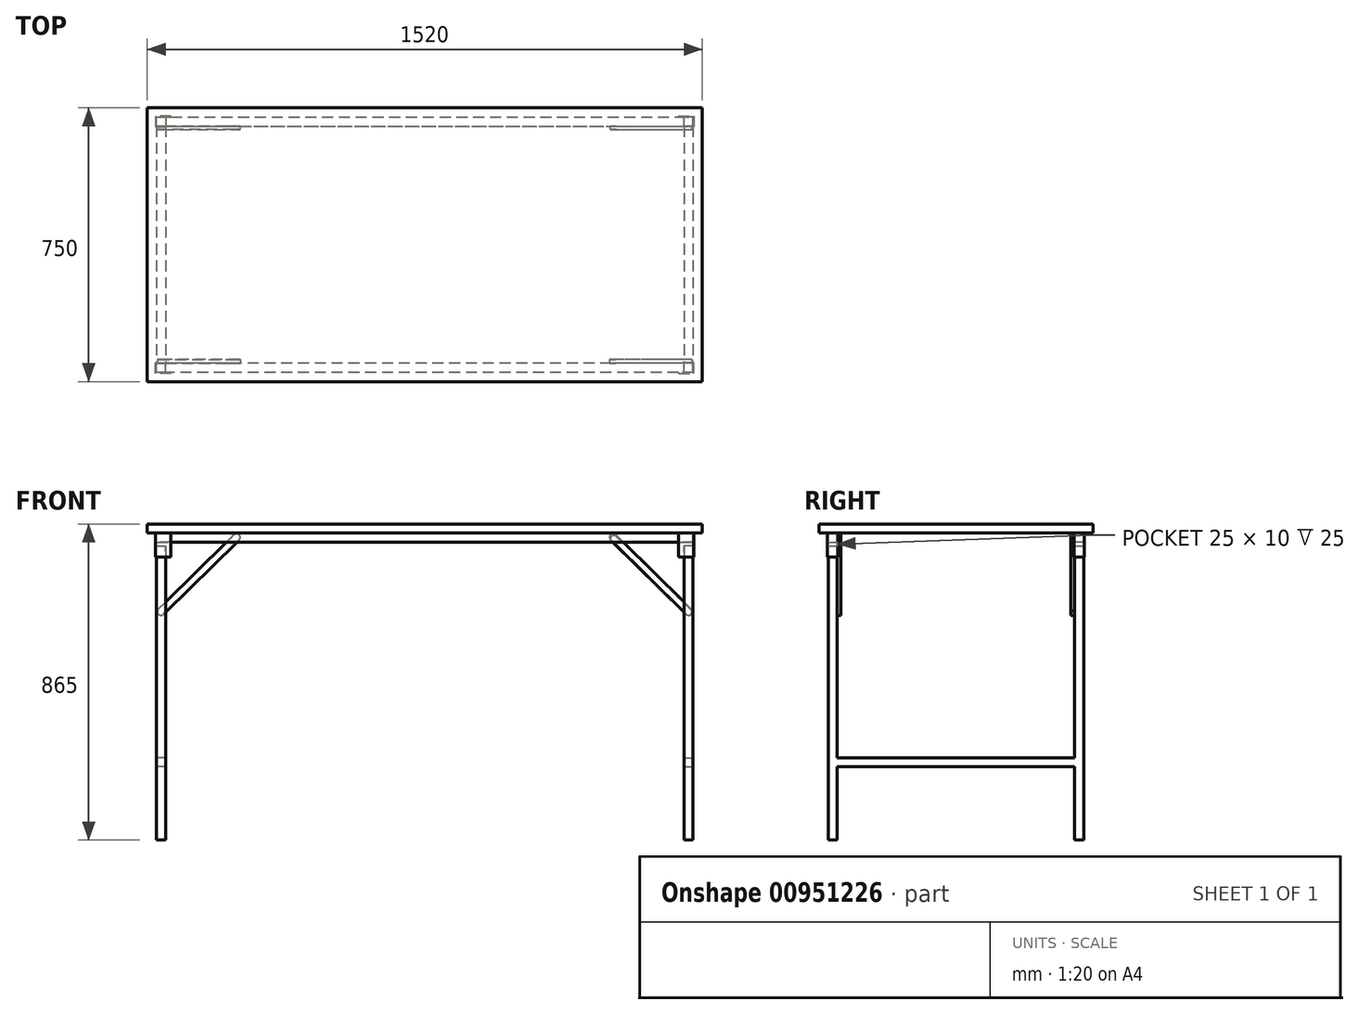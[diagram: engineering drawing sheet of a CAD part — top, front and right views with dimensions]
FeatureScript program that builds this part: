
annotation { "Feature Type Name" : "Feature", "Feature Type Description" : "" }
export const myFeature = defineFeature(function(context is Context, id is Id, definition is map)
    precondition{}
    {
        {
            var Q0;
            Q0=qCreatedBy(makeId("Top.planeOp"),FACE);
            var sketch = newSketch(context, id + "F0", { "sketchPlane" : qUnion([Q0])});
            skLineSegment(sketch, "E0.bottom", {"start": v(0, 0) * mm, "end": v(-1520, 0) * mm});
            skLineSegment(sketch, "E0.top", {"start": v(0, 750) * mm, "end": v(-1520, 750) * mm});
            skLineSegment(sketch, "E0.left", {"start": v(0, 0) * mm, "end": v(0, 750) * mm});
            skLineSegment(sketch, "E0.right", {"start": v(-1520, 0) * mm, "end": v(-1520, 750) * mm});
            skSolve(sketch);
        }
        {
            var Q0;
            Q0=makeQuery(id+"F0.imprint","IMPRINT",FACE,{"disambiguationData":[TD([[makeQuery(id+"F0.imprint","IMPRINT",EDGE,{"derivedFrom":sQuery(id+"F0.wireOp",EDGE,"E0.bottom")}),-1.0]])]});
            extrude(context, id + "F1", {"entities" : qUnion([Q0]), "depth" : 25 * mm, "offsetDistance" : 25 * mm});
        }
        {
            var Q0;
            Q0=makeQuery(id+"F1.opExtrude","CAP_FACE",FACE,{"disambiguationData":[OSD([sQuery(id+"F0.wireOp",EDGE,"E0.bottom"),sQuery(id+"F0.wireOp",EDGE,"E0.top"),sQuery(id+"F0.wireOp",EDGE,"E0.left"),sQuery(id+"F0.wireOp",EDGE,"E0.right")])],"isStart":true});
            var sketch = newSketch(context, id + "F2", { "sketchPlane" : qUnion([Q0])});
            skLineSegment(sketch, "E1.bottom", {"start": v(-25, -25) * mm, "end": v(-1495, -25) * mm});
            skLineSegment(sketch, "E1.top", {"start": v(-25, -50) * mm, "end": v(-1495, -50) * mm});
            skLineSegment(sketch, "E1.left", {"start": v(-25, -25) * mm, "end": v(-25, -50) * mm});
            skLineSegment(sketch, "E1.right", {"start": v(-1495, -25) * mm, "end": v(-1495, -50) * mm});
            skLineSegment(sketch, "E2.bottom", {"start": v(-1495, -700) * mm, "end": v(-25, -700) * mm});
            skLineSegment(sketch, "E2.top", {"start": v(-1495, -725) * mm, "end": v(-25, -725) * mm});
            skLineSegment(sketch, "E2.left", {"start": v(-1495, -700) * mm, "end": v(-1495, -725) * mm});
            skLineSegment(sketch, "E2.right", {"start": v(-25, -700) * mm, "end": v(-25, -725) * mm});
            skSolve(sketch);
        }
        {
            var Q0;
            Q0=qSketchRegion(id+"F2",true);
            extrude(context, id + "F3", {"entities" : qUnion([Q0]), "operationType" : NewBodyOperationType.ADD, "depth" : 25 * mm, "offsetDistance" : 25 * mm});
        }
        {
            var Q0;
            Q0=makeQuery(id+"F1.opExtrude","CAP_FACE",FACE,{"disambiguationData":[OSD([sQuery(id+"F0.wireOp",EDGE,"E0.bottom"),sQuery(id+"F0.wireOp",EDGE,"E0.top"),sQuery(id+"F0.wireOp",EDGE,"E0.left"),sQuery(id+"F0.wireOp",EDGE,"E0.right")])],"isStart":true});
            var sketch = newSketch(context, id + "F4", { "sketchPlane" : qUnion([Q0])});
            skLineSegment(sketch, "E3", {"start": v(-25, -25) * mm, "end": v(-65, -25) * mm});
            skLineSegment(sketch, "E4", {"start": v(-65, -25) * mm, "end": v(-65, -23) * mm});
            skLineSegment(sketch, "E5", {"start": v(-65, -23) * mm, "end": v(-23, -23) * mm});
            skLineSegment(sketch, "E6", {"start": v(-23, -23) * mm, "end": v(-23, -52) * mm});
            skLineSegment(sketch, "E7", {"start": v(-23, -52) * mm, "end": v(-65, -52) * mm});
            skLineSegment(sketch, "E8", {"start": v(-65, -52) * mm, "end": v(-65, -50) * mm});
            skLineSegment(sketch, "E9", {"start": v(-65, -50) * mm, "end": v(-25, -50) * mm});
            skLineSegment(sketch, "E10", {"start": v(-25, -50) * mm, "end": v(-25, -25) * mm});
            skSolve(sketch);
        }
        {
            var Q0;
            Q0=makeQuery(id+"F4.imprint","IMPRINT",FACE,{"disambiguationData":[TD([[makeQuery(id+"F4.imprint","IMPRINT",EDGE,{"derivedFrom":sQuery(id+"F4.wireOp",EDGE,"E3")}),-1.0]])]});
            extrude(context, id + "F5", {"entities" : qUnion([Q0]), "operationType" : NewBodyOperationType.ADD, "depth" : 65 * mm, "offsetDistance" : 25 * mm});
        }
        {
            var Q0;
            Q0=makeQuery(id+"F3.opExtrude","CAP_FACE",FACE,{"disambiguationData":[OSD([sQuery(id+"F2.wireOp",EDGE,"E1.bottom"),sQuery(id+"F2.wireOp",EDGE,"E1.top"),sQuery(id+"F2.wireOp",EDGE,"E1.left"),sQuery(id+"F2.wireOp",EDGE,"E1.right")])],"isStart":false});
            cPlane(context, id + "F6", {"entities" : qUnion([Q0]), "cplaneType" : CPlaneType.OFFSET, "offset" : 10 * mm, "width" : 150 * mm, "height" : 150 * mm});
        }
        {
            var Q0;
            Q0=qCreatedBy(id+"F6.planeOp",FACE);
            var sketch = newSketch(context, id + "F7", { "sketchPlane" : qUnion([Q0])});
            skLineSegment(sketch, "E11.bottom", {"start": v(-25, -25.02) * mm, "end": v(-50, -25.02) * mm});
            skLineSegment(sketch, "E11.top", {"start": v(-25, -50.02) * mm, "end": v(-50, -50.02) * mm});
            skLineSegment(sketch, "E11.left", {"start": v(-25, -25.02) * mm, "end": v(-25, -50.02) * mm});
            skLineSegment(sketch, "E11.right", {"start": v(-50, -25.02) * mm, "end": v(-50, -50.02) * mm});
            skSolve(sketch);
        }
        {
            var Q0;
            Q0=makeQuery(id+"F7.imprint","IMPRINT",FACE,{"disambiguationData":[TD([[makeQuery(id+"F7.imprint","IMPRINT",EDGE,{"derivedFrom":sQuery(id+"F7.wireOp",EDGE,"E11.bottom")}),1.0]])]});
            extrude(context, id + "F8", {"entities" : qUnion([Q0]), "operationType" : NewBodyOperationType.ADD, "depth" : 805 * mm, "offsetDistance" : 25 * mm});
        }
        {
            var Q0;
            Q0=makeQuery(id+"F0.imprint","IMPRINT",FACE,{"disambiguationData":[TD([[makeQuery(id+"F0.imprint","IMPRINT",EDGE,{"derivedFrom":sQuery(id+"F0.wireOp",EDGE,"E0.bottom")}),-1.0]])]});
            var sketch = newSketch(context, id + "F9", { "sketchPlane" : qUnion([Q0])});
            skLineSegment(sketch, "E12", {"start": v(-1495, 25) * mm, "end": v(-1455, 25) * mm});
            skLineSegment(sketch, "E13", {"start": v(-1455, 25) * mm, "end": v(-1455, 23) * mm});
            skLineSegment(sketch, "E14", {"start": v(-1455, 23) * mm, "end": v(-1497, 23) * mm});
            skLineSegment(sketch, "E15", {"start": v(-1497, 23) * mm, "end": v(-1497, 52) * mm});
            skLineSegment(sketch, "E16", {"start": v(-1497, 52) * mm, "end": v(-1455, 52) * mm});
            skLineSegment(sketch, "E17", {"start": v(-1455, 52) * mm, "end": v(-1455, 50) * mm});
            skLineSegment(sketch, "E18", {"start": v(-1455, 50) * mm, "end": v(-1495, 50) * mm});
            skLineSegment(sketch, "E19", {"start": v(-1495, 50) * mm, "end": v(-1495, 25) * mm});
            skLineSegment(sketch, "E20.MirrorCS", {"start": v(-1455, 724.98) * mm, "end": v(-1455, 726.98) * mm});
            skLineSegment(sketch, "E21.MirrorCS", {"start": v(-1455, 697.98) * mm, "end": v(-1455, 699.98) * mm});
            skLineSegment(sketch, "E22.MirrorCS", {"start": v(-1497, 697.98) * mm, "end": v(-1455, 697.98) * mm});
            skLineSegment(sketch, "E23.MirrorCS", {"start": v(-1455, 699.98) * mm, "end": v(-1495, 699.98) * mm});
            skLineSegment(sketch, "E24.MirrorCS", {"start": v(-1495, 724.98) * mm, "end": v(-1455, 724.98) * mm});
            skLineSegment(sketch, "E25.MirrorCS", {"start": v(-1455, 726.98) * mm, "end": v(-1497, 726.98) * mm});
            skLineSegment(sketch, "E26.MirrorCS", {"start": v(-1497, 726.98) * mm, "end": v(-1497, 697.98) * mm});
            skLineSegment(sketch, "E27.MirrorCS", {"start": v(-1495, 699.98) * mm, "end": v(-1495, 724.98) * mm});
            skLineSegment(sketch, "E28.MirrorCS", {"start": v(-65.05, 724.98) * mm, "end": v(-65.05, 726.98) * mm});
            skLineSegment(sketch, "E29.MirrorCS", {"start": v(-65.05, 697.98) * mm, "end": v(-65.05, 699.98) * mm});
            skLineSegment(sketch, "E30.MirrorCS", {"start": v(-23.05, 726.98) * mm, "end": v(-23.05, 697.98) * mm});
            skLineSegment(sketch, "E31.MirrorCS", {"start": v(-65.05, 699.98) * mm, "end": v(-25.05, 699.98) * mm});
            skLineSegment(sketch, "E32.MirrorCS", {"start": v(-25.05, 699.98) * mm, "end": v(-25.05, 724.98) * mm});
            skLineSegment(sketch, "E33.MirrorCS", {"start": v(-65.05, 726.98) * mm, "end": v(-23.05, 726.98) * mm});
            skLineSegment(sketch, "E34.MirrorCS", {"start": v(-25.05, 724.98) * mm, "end": v(-65.05, 724.98) * mm});
            skLineSegment(sketch, "E35.MirrorCS", {"start": v(-23.05, 697.98) * mm, "end": v(-65.05, 697.98) * mm});
            skSolve(sketch);
        }
        {
            var Q0;
            Q0=makeQuery(id+"F9.imprint","IMPRINT",FACE,{"disambiguationData":[TD([[makeQuery(id+"F9.imprint","IMPRINT",EDGE,{"derivedFrom":sQuery(id+"F9.wireOp",EDGE,"E20.MirrorCS")}),1.0]])]});
            var Q1;
            Q1=makeQuery(id+"F9.imprint","IMPRINT",FACE,{"disambiguationData":[TD([[makeQuery(id+"F9.imprint","IMPRINT",EDGE,{"derivedFrom":sQuery(id+"F9.wireOp",EDGE,"E28.MirrorCS")}),-1.0]])]});
            var Q2;
            Q2=makeQuery(id+"F9.imprint","IMPRINT",FACE,{"disambiguationData":[TD([[makeQuery(id+"F9.imprint","IMPRINT",EDGE,{"derivedFrom":sQuery(id+"F9.wireOp",EDGE,"E12")}),-1.0]])]});
            extrude(context, id + "F10", {"entities" : qUnion([Q0, Q1, Q2]), "operationType" : NewBodyOperationType.ADD, "oppositeDirection" : true, "depth" : 65 * mm, "offsetDistance" : 25 * mm});
        }
        {
            var Q0;
            Q0=makeQuery(id+"F3.opExtrude","CAP_FACE",FACE,{"disambiguationData":[OSD([sQuery(id+"F2.wireOp",EDGE,"E1.bottom"),sQuery(id+"F2.wireOp",EDGE,"E1.top"),sQuery(id+"F2.wireOp",EDGE,"E1.left"),sQuery(id+"F2.wireOp",EDGE,"E1.right")])],"isStart":false});
            cPlane(context, id + "F11", {"entities" : qUnion([Q0]), "cplaneType" : CPlaneType.OFFSET, "offset" : 10 * mm, "width" : 150 * mm, "height" : 150 * mm});
        }
        {
            var Q0;
            Q0=qCreatedBy(id+"F11.planeOp",FACE);
            var sketch = newSketch(context, id + "F12", { "sketchPlane" : qUnion([Q0])});
            skLineSegment(sketch, "E36.bottom", {"start": v(-1470, -25) * mm, "end": v(-1495, -25) * mm});
            skLineSegment(sketch, "E36.top", {"start": v(-1470, -50) * mm, "end": v(-1495, -50) * mm});
            skLineSegment(sketch, "E36.left", {"start": v(-1470, -25) * mm, "end": v(-1470, -50) * mm});
            skLineSegment(sketch, "E36.right", {"start": v(-1495, -25) * mm, "end": v(-1495, -50) * mm});
            skSolve(sketch);
        }
        {
            var Q0;
            Q0=makeQuery(id+"F12.imprint","IMPRINT",FACE,{"disambiguationData":[TD([[makeQuery(id+"F12.imprint","IMPRINT",EDGE,{"derivedFrom":sQuery(id+"F12.wireOp",EDGE,"E36.bottom")}),1.0]])]});
            extrude(context, id + "F13", {"entities" : qUnion([Q0]), "operationType" : NewBodyOperationType.ADD, "depth" : 805 * mm, "offsetDistance" : 25 * mm});
        }
        {
            var Q0;
            Q0=makeQuery(id+"F3.opExtrude","CAP_FACE",FACE,{"disambiguationData":[OSD([sQuery(id+"F2.wireOp",EDGE,"E2.bottom"),sQuery(id+"F2.wireOp",EDGE,"E2.top"),sQuery(id+"F2.wireOp",EDGE,"E2.left"),sQuery(id+"F2.wireOp",EDGE,"E2.right")])],"isStart":false});
            cPlane(context, id + "F14", {"entities" : qUnion([Q0]), "cplaneType" : CPlaneType.OFFSET, "offset" : 10 * mm, "width" : 150 * mm, "height" : 150 * mm});
        }
        {
            var Q0;
            Q0=qCreatedBy(id+"F14.planeOp",FACE);
            var sketch = newSketch(context, id + "F15", { "sketchPlane" : qUnion([Q0])});
            skLineSegment(sketch, "E37.bottom", {"start": v(-25, -700) * mm, "end": v(-50, -700) * mm});
            skLineSegment(sketch, "E37.top", {"start": v(-25, -725) * mm, "end": v(-50, -725) * mm});
            skLineSegment(sketch, "E37.left", {"start": v(-25, -700) * mm, "end": v(-25, -725) * mm});
            skLineSegment(sketch, "E37.right", {"start": v(-50, -700) * mm, "end": v(-50, -725) * mm});
            skLineSegment(sketch, "E38.bottom", {"start": v(-1495, -725) * mm, "end": v(-1470, -725) * mm});
            skLineSegment(sketch, "E38.top", {"start": v(-1495, -700) * mm, "end": v(-1470, -700) * mm});
            skLineSegment(sketch, "E38.left", {"start": v(-1495, -725) * mm, "end": v(-1495, -700) * mm});
            skLineSegment(sketch, "E38.right", {"start": v(-1470, -725) * mm, "end": v(-1470, -700) * mm});
            skSolve(sketch);
        }
        {
            var Q0;
            Q0=qSketchRegion(id+"F15",true);
            extrude(context, id + "F16", {"entities" : qUnion([Q0]), "operationType" : NewBodyOperationType.ADD, "depth" : 805 * mm, "offsetDistance" : 25 * mm});
        }
        {
            var Q0;
            Q0=makeQuery(id+"F8.opExtrude","SWEPT_FACE",FACE,{"disambiguationData":[OSD([sQuery(id+"F7.wireOp",EDGE,"E11.top")])]});
            cPlane(context, id + "F17", {"entities" : qUnion([Q0]), "cplaneType" : CPlaneType.OFFSET, "offset" : 0 * mm, "width" : 150 * mm, "height" : 150 * mm});
        }
        {
            var Q0;
            Q0=qCreatedBy(id+"F17.planeOp",FACE);
            var sketch = newSketch(context, id + "F18", { "sketchPlane" : qUnion([Q0])});
            skLineSegment(sketch, "E39.bottom", {"start": v(25, -615) * mm, "end": v(50, -615) * mm});
            skLineSegment(sketch, "E39.top", {"start": v(25, -640) * mm, "end": v(50, -640) * mm});
            skLineSegment(sketch, "E39.left", {"start": v(25, -615) * mm, "end": v(25, -640) * mm});
            skLineSegment(sketch, "E39.right", {"start": v(50, -615) * mm, "end": v(50, -640) * mm});
            skSolve(sketch);
        }
        {
            var Q0;
            Q0=makeQuery(id+"F18.imprint","IMPRINT",FACE,{"disambiguationData":[TD([[makeQuery(id+"F18.imprint","IMPRINT",EDGE,{"derivedFrom":sQuery(id+"F18.wireOp",EDGE,"E39.bottom")}),-1.0]])]});
            extrude(context, id + "F19", {"entities" : qUnion([Q0]), "operationType" : NewBodyOperationType.ADD, "depth" : 650 * mm, "offsetDistance" : 25 * mm});
        }
        {
            var Q0;
            Q0=makeQuery(id+"F13.opExtrude","SWEPT_FACE",FACE,{"disambiguationData":[OSD([sQuery(id+"F12.wireOp",EDGE,"E36.top")])]});
            cPlane(context, id + "F20", {"entities" : qUnion([Q0]), "cplaneType" : CPlaneType.OFFSET, "offset" : 0 * mm, "width" : 150 * mm, "height" : 150 * mm});
        }
        {
            var Q0;
            Q0=qCreatedBy(id+"F20.planeOp",FACE);
            var sketch = newSketch(context, id + "F21", { "sketchPlane" : qUnion([Q0])});
            skLineSegment(sketch, "E40.0", {"start": v(1470, -840) * mm, "end": v(1470, -65) * mm});
            skLineSegment(sketch, "E41.0.0", {"start": v(1495, -65) * mm, "end": v(1470, -65) * mm});
            skLineSegment(sketch, "E41.0.1", {"start": v(1470, -65) * mm, "end": v(1470, -840) * mm});
            skLineSegment(sketch, "E41.0.2", {"start": v(1470, -840) * mm, "end": v(1495, -840) * mm});
            skLineSegment(sketch, "E41.0.3", {"start": v(1495, -840) * mm, "end": v(1495, -65) * mm});
            skLineSegment(sketch, "E42.bottom", {"start": v(1470, -615) * mm, "end": v(1495, -615) * mm});
            skLineSegment(sketch, "E42.top", {"start": v(1470, -640) * mm, "end": v(1495, -640) * mm});
            skLineSegment(sketch, "E42.left", {"start": v(1470, -615) * mm, "end": v(1470, -640) * mm});
            skLineSegment(sketch, "E42.right", {"start": v(1495, -615) * mm, "end": v(1495, -640) * mm});
            skSolve(sketch);
        }
        {
            var Q0;
            Q0=makeQuery(id+"F21.imprint","IMPRINT",FACE,{"disambiguationData":[TD([[makeQuery(id+"F21.imprint","IMPRINT",EDGE,{"derivedFrom":sQuery(id+"F21.wireOp",EDGE,"E42.bottom")}),-1.0]])]});
            extrude(context, id + "F22", {"entities" : qUnion([Q0]), "operationType" : NewBodyOperationType.ADD, "depth" : 650 * mm, "offsetDistance" : 25 * mm});
        }
        {
            var Q0;
            {var subQ0=sQuery(id+"F9.wireOp",EDGE,"E32.MirrorCS");var subQ3=sQuery(id+"F15.wireOp",EDGE,"E37.bottom");Q0=makeQuery(id+"F19.boolean.opBoolean","SPLIT",FACE,{"disambiguationData":[TD([makeQuery(id+"F10.opExtrude","SWEPT_FACE",FACE,{"disambiguationData":[OSD([subQ0])]})])],"derivedFrom":makeQuery(id+"F16.opExtrude","SWEPT_FACE",FACE,{"disambiguationData":[OSD([subQ3])]})});}
            var sketch = newSketch(context, id + "F23", { "sketchPlane" : qUnion([Q0])});
            skPoint(sketch, "E43", {"position": v(-37.5, -215) * mm});
            skPoint(sketch, "E44", {"position": v(-243.05, -12.5) * mm});
            skPoint(sketch, "E45", {"position": v(-118.3, 56.79) * mm});
            skLineSegment(sketch, "E46", {"start": v(-234.62, -9.28) * mm, "end": v(-27.8, -212.56) * mm});
            skLineSegment(sketch, "E47", {"start": v(-251.33, -18.85) * mm, "end": v(-44.5, -222.13) * mm});
            skArc(sketch, "E48", {"start": v(-44.5, -222.13) * mm, "mid": v(-32.53, -223.68) * mm, "end": v(-27.8, -212.56) * mm});
            skArc(sketch, "E49", {"start": v(-234.62, -9.28) * mm, "mid": v(-246.6, -7.73) * mm, "end": v(-251.33, -18.85) * mm});
            skSolve(sketch);
        }
        {
            var Q0;
            {var subQ0=sQuery(id+"F23.wireOp",EDGE,"E49");Q0=makeQuery(id+"F23.imprint","IMPRINT",FACE,{"disambiguationData":[TD([[makeQuery(id+"F23.imprint","IMPRINT",EDGE,{"derivedFrom":subQ0}),1.0]])]});}
            var Q1;
            {var subQ0=sQuery(id+"F23.wireOp",EDGE,"E48");Q1=makeQuery(id+"F23.imprint","IMPRINT",FACE,{"disambiguationData":[TD([[makeQuery(id+"F23.imprint","IMPRINT",EDGE,{"derivedFrom":subQ0}),1.0]])]});}
            extrude(context, id + "F24", {"entities" : qUnion([Q0, Q1]), "operationType" : NewBodyOperationType.ADD, "depth" : 10 * mm, "offsetDistance" : 25 * mm});
        }
        {
            var Q0;
            Q0=makeQuery(id+"F19.boolean.opBoolean","SPLIT",FACE,{"disambiguationData":[TD([makeQuery(id+"F19.opExtrude","SWEPT_FACE",FACE,{"disambiguationData":[OSD([sQuery(id+"F18.wireOp",EDGE,"E39.bottom")])]})])],"derivedFrom":makeQuery(id+"F8.opExtrude","SWEPT_FACE",FACE,{"disambiguationData":[OSD([sQuery(id+"F7.wireOp",EDGE,"E11.top")])]})});
            var sketch = newSketch(context, id + "F25", { "sketchPlane" : qUnion([Q0])});
            skPoint(sketch, "E50", {"position": v(37.5, -215) * mm});
            skPoint(sketch, "E51", {"position": v(243, -12.5) * mm});
            skLineSegment(sketch, "E52", {"start": v(44.52, -222.12) * mm, "end": v(250.98, -18.46) * mm});
            skLineSegment(sketch, "E53", {"start": v(30.48, -207.88) * mm, "end": v(236.93, -4.22) * mm});
            skLineSegment(sketch, "E54", {"start": v(43.27, -207.6) * mm, "end": v(43.27, -207.6) * mm});
            skArc(sketch, "E55", {"start": v(30.48, -207.88) * mm, "mid": v(30.38, -222.02) * mm, "end": v(44.52, -222.12) * mm});
            skArc(sketch, "E56", {"start": v(250.98, -18.46) * mm, "mid": v(251.08, -4.32) * mm, "end": v(236.93, -4.22) * mm});
            skSolve(sketch);
        }
        {
            var Q0;
            {var subQ0=sQuery(id+"F25.wireOp",EDGE,"E56");Q0=makeQuery(id+"F25.imprint","IMPRINT",FACE,{"disambiguationData":[TD([[makeQuery(id+"F25.imprint","IMPRINT",EDGE,{"derivedFrom":subQ0}),1.0]])]});}
            var Q1;
            {var subQ0=sQuery(id+"F25.wireOp",EDGE,"E55");Q1=makeQuery(id+"F25.imprint","IMPRINT",FACE,{"disambiguationData":[TD([[makeQuery(id+"F25.imprint","IMPRINT",EDGE,{"derivedFrom":subQ0}),1.0]])]});}
            extrude(context, id + "F26", {"entities" : qUnion([Q0, Q1]), "depth" : 10 * mm, "offsetDistance" : 25 * mm});
        }
        {
            var Q0;
            {var subQ2=sQuery(id+"F15.wireOp",EDGE,"E38.top");var subQ3=sQuery(id+"F9.wireOp",EDGE,"E27.MirrorCS");Q0=makeQuery(id+"F22.boolean.opBoolean","SPLIT",FACE,{"disambiguationData":[TD([makeQuery(id+"F10.opExtrude","SWEPT_FACE",FACE,{"disambiguationData":[OSD([subQ3])]})])],"derivedFrom":makeQuery(id+"F16.opExtrude","SWEPT_FACE",FACE,{"disambiguationData":[OSD([subQ2])]})});}
            cPlane(context, id + "F27", {"entities" : qUnion([Q0]), "cplaneType" : CPlaneType.OFFSET, "offset" : 0 * mm, "width" : 150 * mm, "height" : 150 * mm});
        }
        {
            var Q0;
            Q0=qCreatedBy(id+"F27.planeOp",FACE);
            var sketch = newSketch(context, id + "F28", { "sketchPlane" : qUnion([Q0])});
            skPoint(sketch, "E57", {"position": v(-1482.5, -215) * mm});
            skPoint(sketch, "E58", {"position": v(-1277, -12.5) * mm});
            skLineSegment(sketch, "E59", {"start": v(-1282.53, -4.73) * mm, "end": v(-1489.5, -207.86) * mm});
            skLineSegment(sketch, "E60", {"start": v(-1475.5, -222.14) * mm, "end": v(-1268.52, -19) * mm});
            skArc(sketch, "E61", {"start": v(-1489.5, -207.86) * mm, "mid": v(-1489.64, -222) * mm, "end": v(-1475.5, -222.14) * mm});
            skArc(sketch, "E62", {"start": v(-1268.52, -19) * mm, "mid": v(-1268.39, -4.87) * mm, "end": v(-1282.53, -4.73) * mm});
            skSolve(sketch);
        }
        {
            var Q0;
            Q0=makeQuery(id+"F28.imprint","IMPRINT",FACE,{"disambiguationData":[TD([[makeQuery(id+"F28.imprint","IMPRINT",EDGE,{"derivedFrom":sQuery(id+"F28.wireOp",EDGE,"E59")}),1.0]])]});
            extrude(context, id + "F29", {"entities" : qUnion([Q0]), "operationType" : NewBodyOperationType.ADD, "depth" : 10 * mm, "offsetDistance" : 25 * mm});
        }
        {
            var Q0;
            {var subQ0=sQuery(id+"F21.wireOp",EDGE,"E41.0.0");Q0=makeQuery(id+"F21.imprint","IMPRINT",FACE,{"disambiguationData":[TD([[makeQuery(id+"F21.imprint","IMPRINT",EDGE,{"derivedFrom":subQ0}),1.0]])]});}
            var sketch = newSketch(context, id + "F30", { "sketchPlane" : qUnion([Q0])});
            skLineSegment(sketch, "E63", {"start": v(1489.5, -207.85) * mm, "end": v(1282.21, -5.04) * mm});
            skLineSegment(sketch, "E64", {"start": v(1268.23, -19.33) * mm, "end": v(1475.5, -222.15) * mm});
            skArc(sketch, "E65", {"start": v(1475.5, -222.15) * mm, "mid": v(1489.65, -222) * mm, "end": v(1489.5, -207.85) * mm});
            skArc(sketch, "E66", {"start": v(1282.21, -5.04) * mm, "mid": v(1268.07, -5.19) * mm, "end": v(1268.23, -19.33) * mm});
            skSolve(sketch);
        }
        {
            var Q0;
            {var subQ0=sQuery(id+"F30.wireOp",EDGE,"E65");Q0=makeQuery(id+"F30.imprint","IMPRINT",FACE,{"disambiguationData":[TD([[makeQuery(id+"F30.imprint","IMPRINT",EDGE,{"derivedFrom":subQ0}),1.0]])]});}
            var Q1;
            {var subQ0=sQuery(id+"F30.wireOp",EDGE,"E66");Q1=makeQuery(id+"F30.imprint","IMPRINT",FACE,{"disambiguationData":[TD([[makeQuery(id+"F30.imprint","IMPRINT",EDGE,{"derivedFrom":subQ0}),1.0]])]});}
            extrude(context, id + "F31", {"entities" : qUnion([Q0, Q1]), "operationType" : NewBodyOperationType.ADD, "depth" : 10 * mm, "offsetDistance" : 25 * mm});
        }
    });
